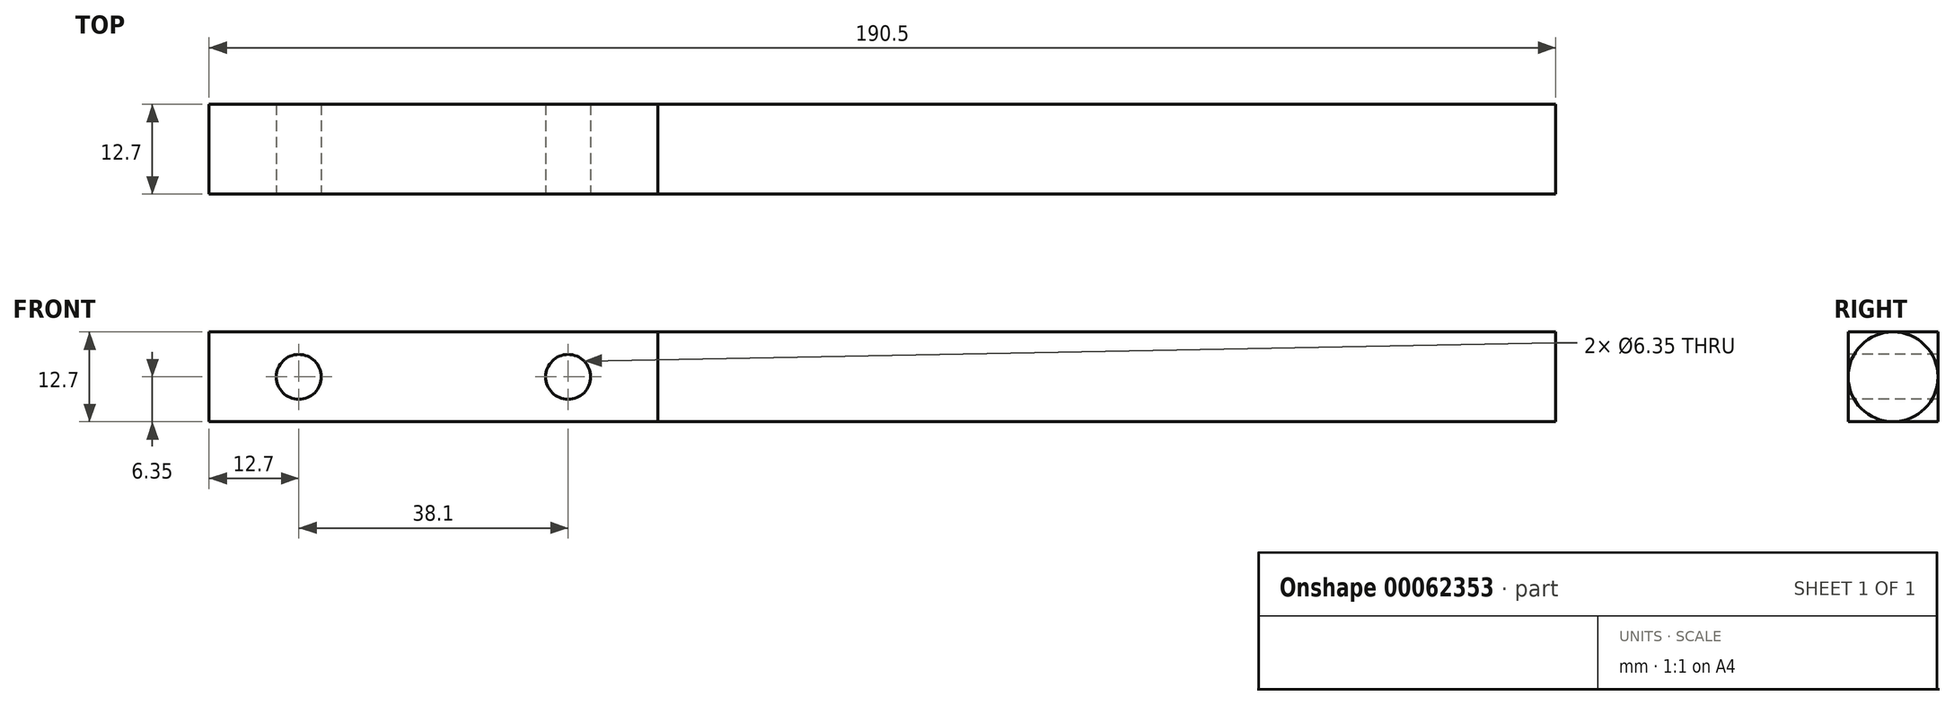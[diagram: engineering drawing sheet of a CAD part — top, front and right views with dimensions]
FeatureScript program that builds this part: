
annotation { "Feature Type Name" : "Feature", "Feature Type Description" : "" }
export const myFeature = defineFeature(function(context is Context, id is Id, definition is map)
    precondition{}
    {
        {
            var Q0;
            Q0=qCreatedBy(makeId("Right.planeOp"),FACE);
            var sketch = newSketch(context, id + "F0", { "sketchPlane" : qUnion([Q0])});
            skLineSegment(sketch, "E0.rect.bottom", {"start": v(6.35, 6.35) * mm, "end": v(-6.35, 6.35) * mm});
            skLineSegment(sketch, "E0.rect.top", {"start": v(6.35, -6.35) * mm, "end": v(-6.35, -6.35) * mm});
            skLineSegment(sketch, "E0.rect.left", {"start": v(6.35, 6.35) * mm, "end": v(6.35, -6.35) * mm});
            skLineSegment(sketch, "E0.rect.right", {"start": v(-6.35, 6.35) * mm, "end": v(-6.35, -6.35) * mm});
            skPoint(sketch, "E0.rect.middle", {"position": v(0, 0) * mm});
            skSolve(sketch);
        }
        {
            var Q0;
            Q0=makeQuery(id+"F0.imprint","IMPRINT",FACE,{"disambiguationData":[TD([[makeQuery(id+"F0.imprint","IMPRINT",EDGE,{"derivedFrom":sQuery(id+"F0.wireOp",EDGE,"E0.rect.bottom")}),1.0]])]});
            extrude(context, id + "F1", {"entities" : qUnion([Q0]), "oppositeDirection" : true, "depth" : 63.5 * mm});
        }
        {
            var Q0;
            Q0=qCreatedBy(makeId("Right.planeOp"),FACE);
            var sketch = newSketch(context, id + "F2", { "sketchPlane" : qUnion([Q0])});
            skCircle(sketch, "E1", {"center": v(0, 0) * mm, "radius": 6.35 * mm});
            skSolve(sketch);
        }
        {
            var Q0;
            Q0=makeQuery(id+"F2.imprint","IMPRINT",FACE,{"disambiguationData":[TD([[makeQuery(id+"F2.imprint","IMPRINT",EDGE,{"derivedFrom":sQuery(id+"F2.wireOp",EDGE,"E1")}),1.0]])]});
            extrude(context, id + "F3", {"entities" : qUnion([Q0]), "operationType" : NewBodyOperationType.ADD, "depth" : 127 * mm});
        }
        {
            var Q0;
            Q0=makeQuery(id+"F1.opExtrude","SWEPT_FACE",FACE,{"disambiguationData":[OSD([sQuery(id+"F0.wireOp",EDGE,"E0.rect.right")])]});
            var sketch = newSketch(context, id + "F4", { "sketchPlane" : qUnion([Q0])});
            skCircle(sketch, "E2", {"center": v(-50.8, 0) * mm, "radius": 3.18 * mm});
            skCircle(sketch, "E3", {"center": v(-12.7, 0) * mm, "radius": 3.18 * mm});
            skSolve(sketch);
        }
        {
            var Q0;
            Q0=sQuery(id+"F4.wireOp",VERTEX,"E2.center");
            var Q1;
            Q1=sQuery(id+"F4.wireOp",VERTEX,"E3.center");
            var Q2;
            Q2=makeQuery(id+"F1.opExtrude","SWEPT_BODY",BODY,{"disambiguationData":[OSD([sQuery(id+"F0.wireOp",EDGE,"E0.rect.bottom"),sQuery(id+"F0.wireOp",EDGE,"E0.rect.top"),sQuery(id+"F0.wireOp",EDGE,"E0.rect.left"),sQuery(id+"F0.wireOp",EDGE,"E0.rect.right")])]});
            hole(context, id + "F5", {"style" : HoleStyle.SIMPLE, "holeDiameter" : 6.35 * mm, "endStyle" : HoleEndStyle.THROUGH, "locations" : qUnion([Q0, Q1]), "scope" : qUnion([Q2])});
        }
    });
